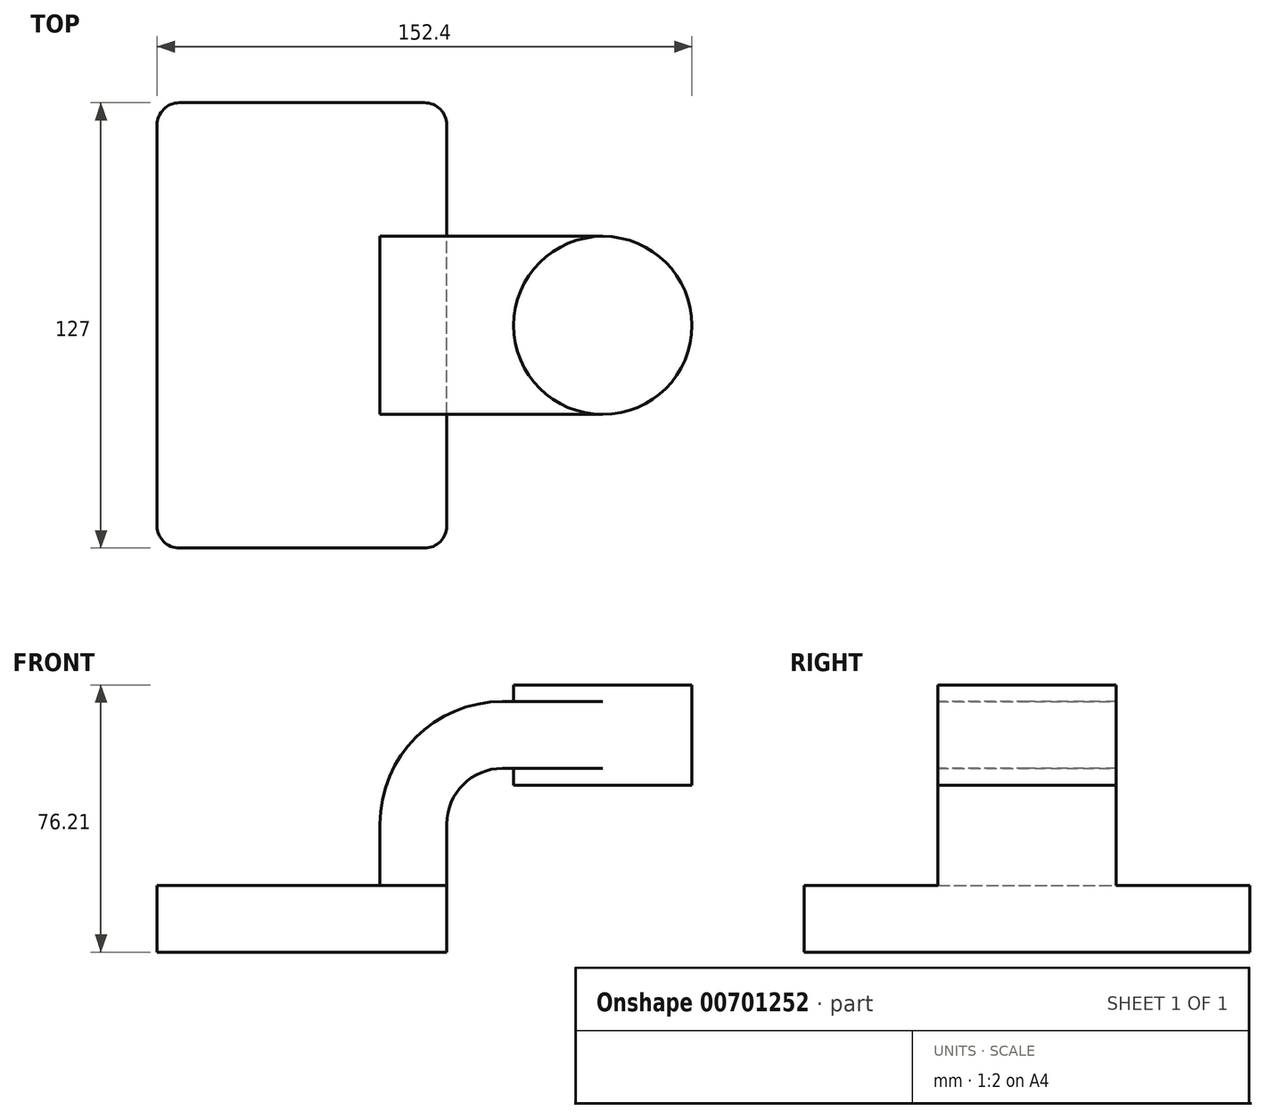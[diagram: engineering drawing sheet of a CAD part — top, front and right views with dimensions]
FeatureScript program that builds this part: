
annotation { "Feature Type Name" : "Feature", "Feature Type Description" : "" }
export const myFeature = defineFeature(function(context is Context, id is Id, definition is map)
    precondition{}
    {
        {
            var Q0;
            Q0=qCreatedBy(makeId("Front.planeOp"),FACE);
            var sketch = newSketch(context, id + "F0", { "sketchPlane" : qUnion([Q0])});
            skLineSegment(sketch, "E0.bottom", {"start": v(-41.27, 9.52) * mm, "end": v(41.27, 9.53) * mm});
            skLineSegment(sketch, "E0.top", {"start": v(-41.27, -9.53) * mm, "end": v(41.27, -9.53) * mm});
            skLineSegment(sketch, "E0.left", {"start": v(-41.27, 9.52) * mm, "end": v(-41.27, -9.53) * mm});
            skLineSegment(sketch, "E0.right", {"start": v(41.27, 9.53) * mm, "end": v(41.28, -9.52) * mm});
            skPoint(sketch, "E0.middle", {"position": v(0, 0) * mm});
            skLineSegment(sketch, "E1.bottom", {"start": v(60.33, 38.1) * mm, "end": v(111.13, 38.1) * mm});
            skLineSegment(sketch, "E1.top", {"start": v(60.32, 66.68) * mm, "end": v(111.12, 66.68) * mm});
            skLineSegment(sketch, "E1.left", {"start": v(60.32, 38.1) * mm, "end": v(60.32, 66.68) * mm});
            skLineSegment(sketch, "E1.right", {"start": v(111.13, 38.1) * mm, "end": v(111.12, 66.68) * mm});
            skPoint(sketch, "E1.middle", {"position": v(85.72, 52.39) * mm});
            skLineSegment(sketch, "E2", {"start": v(41.27, 9.53) * mm, "end": v(41.27, 27) * mm});
            skArc(sketch, "E3", {"start": v(41.27, 27) * mm, "mid": v(45.92, 38.23) * mm, "end": v(57.15, 42.88) * mm});
            skLineSegment(sketch, "E4", {"start": v(57.15, 42.88) * mm, "end": v(85.72, 42.88) * mm});
            skLineSegment(sketch, "E5.0", {"start": v(57.15, 61.93) * mm, "end": v(85.72, 61.93) * mm});
            skArc(sketch, "E5.1", {"start": v(22.22, 27) * mm, "mid": v(32.45, 51.7) * mm, "end": v(57.15, 61.93) * mm});
            skLineSegment(sketch, "E5.2", {"start": v(22.22, 9.53) * mm, "end": v(22.22, 27) * mm});
            skLineSegment(sketch, "E6", {"start": v(85.72, 38.1) * mm, "end": v(85.72, 61.93) * mm});
            skFitSpline(sketch, "E7", {"points": [v(-41.28, 9.52) * mm, v(57.15, 61.93) * mm], "startDerivative": vector(1.4, 104.52) * mm, "endDerivative": vector(132.77, -4.93) * mm});
            skLineSegment(sketch, "E8", {"start": v(85.72, 61.93) * mm, "end": v(85.72, 66.68) * mm});
            skSolve(sketch);
        }
        {
            var Q0;
            Q0=makeQuery(id+"F0.imprint","IMPRINT",FACE,{"disambiguationData":[TD([[makeQuery(id+"F0.imprint","IMPRINT",EDGE,{"derivedFrom":sQuery(id+"F0.wireOp",EDGE,"E0.top")}),1.0]])]});
            extrude(context, id + "F1", {"entities" : qUnion([Q0]), "endBound" : BoundingType.SYMMETRIC, "depth" : 127 * mm, "offsetDistance" : 25.4 * mm});
        }
        {
            var Q0;
            {var subQ1=sQuery(id+"F0.wireOp",EDGE,"E2");Q0=makeQuery(id+"F0.imprint","IMPRINT",FACE,{"disambiguationData":[TD([[makeQuery(id+"F0.imprint","IMPRINT",EDGE,{"derivedFrom":subQ1}),1.0]])]});}
            var Q1;
            {var subQ0=sQuery(id+"F0.wireOp",EDGE,"E4");var subQ1=sQuery(id+"F0.wireOp",EDGE,"E1.left");var subQ2=makeQuery(id+"F0.imprint","INTERSECT",VERTEX,{"derivedFrom":[subQ1,subQ0]});Q1=makeQuery(id+"F0.imprint","IMPRINT",FACE,{"disambiguationData":[TD([[makeQuery(id+"F0.imprint","IMPRINT",EDGE,{"disambiguationData":[TD([[subQ2,-1.0]])],"derivedFrom":subQ1}),-1.0]])]});}
            extrude(context, id + "F2", {"entities" : qUnion([Q0, Q1]), "operationType" : NewBodyOperationType.ADD, "endBound" : BoundingType.SYMMETRIC, "depth" : 50.8 * mm, "offsetDistance" : 25.4 * mm});
        }
        {
            var Q0;
            Q0=makeQuery(id+"F0.imprint","IMPRINT",FACE,{"disambiguationData":[TD([[makeQuery(id+"F0.imprint","IMPRINT",EDGE,{"derivedFrom":sQuery(id+"F0.wireOp",EDGE,"E5.1")}),1.0]])]});
            extrude(context, id + "F3", {"entities" : qUnion([Q0]), "operationType" : NewBodyOperationType.ADD, "endBound" : BoundingType.SYMMETRIC, "depth" : 15.88 * mm, "offsetDistance" : 25.4 * mm});
        }
        {
            var Q0;
            {var subQ0=sQuery(id+"F0.wireOp",EDGE,"E1.right");Q0=makeQuery(id+"F0.imprint","IMPRINT",FACE,{"disambiguationData":[TD([[makeQuery(id+"F0.imprint","IMPRINT",EDGE,{"derivedFrom":subQ0}),1.0]])]});}
            var Q1;
            Q1=sQuery(id+"F0.wireOp",EDGE,"E8");
            revolve(context, id + "F4", {"operationType" : NewBodyOperationType.ADD, "entities" : qUnion([Q0]), "axis" : qUnion([Q1]), "revolveType" : RevolveType.FULL});
        }
        {
            var Q0;
            Q0=makeQuery(id+"F1.opExtrude","CAP_EDGE",EDGE,{"disambiguationData":[OSD([sQuery(id+"F0.wireOp",EDGE,"E0.right")])],"isStart":false});
            var Q1;
            Q1=makeQuery(id+"F1.opExtrude","CAP_EDGE",EDGE,{"disambiguationData":[OSD([sQuery(id+"F0.wireOp",EDGE,"E0.left")])],"isStart":false});
            var Q2;
            Q2=makeQuery(id+"F1.opExtrude","CAP_EDGE",EDGE,{"disambiguationData":[OSD([sQuery(id+"F0.wireOp",EDGE,"E0.left")])],"isStart":true});
            var Q3;
            Q3=makeQuery(id+"F1.opExtrude","CAP_EDGE",EDGE,{"disambiguationData":[OSD([sQuery(id+"F0.wireOp",EDGE,"E0.right")])],"isStart":true});
            fillet(context, id + "F5", {"entities" : qUnion([Q0, Q1, Q2, Q3]), "radius" : 6.35 * mm, "tangentPropagation" : true, "allowEdgeOverflow" : false});
        }
    });
